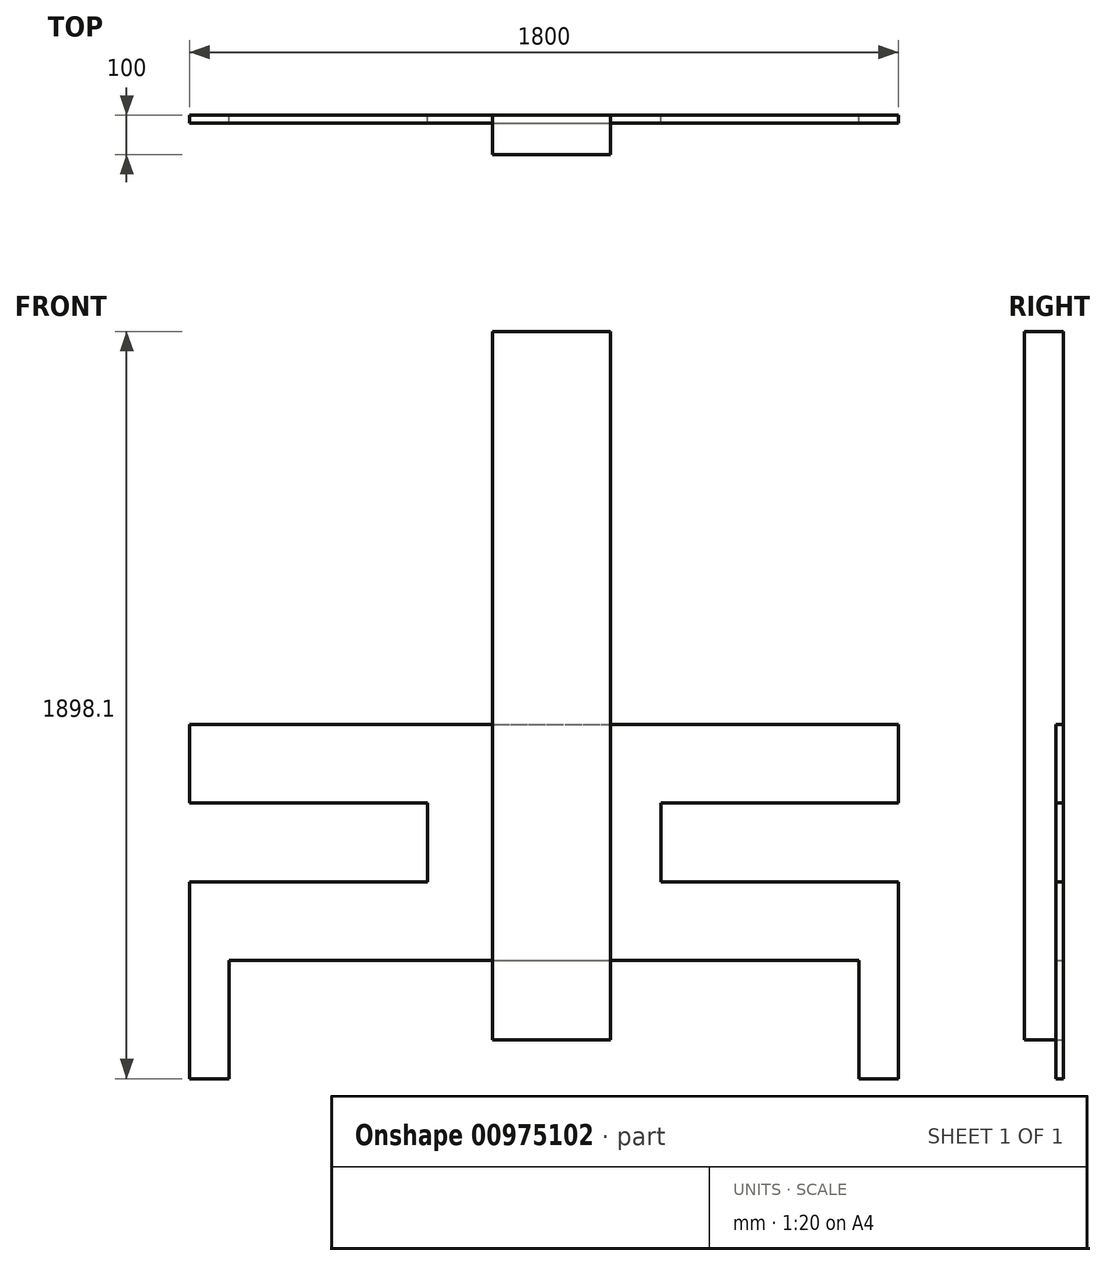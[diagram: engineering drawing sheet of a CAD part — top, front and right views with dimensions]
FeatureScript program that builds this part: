
annotation { "Feature Type Name" : "Feature", "Feature Type Description" : "" }
export const myFeature = defineFeature(function(context is Context, id is Id, definition is map)
    precondition{}
    {
        {
            var Q0;
            Q0=qCreatedBy(makeId("Front.planeOp"),FACE);
            var sketch = newSketch(context, id + "F0", { "sketchPlane" : qUnion([Q0])});
            skLineSegment(sketch, "E0.bottom", {"start": v(-150, 900) * mm, "end": v(150, 900) * mm});
            skLineSegment(sketch, "E0.top", {"start": v(-150, -900) * mm, "end": v(150, -900) * mm});
            skLineSegment(sketch, "E0.left", {"start": v(-150, 900) * mm, "end": v(-150, -900) * mm});
            skLineSegment(sketch, "E0.right", {"start": v(150, 900) * mm, "end": v(150, -900) * mm});
            skPoint(sketch, "E0.middle", {"position": v(0, 0) * mm});
            skSolve(sketch);
        }
        {
            var Q0;
            Q0=makeQuery(id+"F0.imprint","IMPRINT",FACE,{"disambiguationData":[TD([[makeQuery(id+"F0.imprint","IMPRINT",EDGE,{"derivedFrom":sQuery(id+"F0.wireOp",EDGE,"E0.bottom")}),-1.0]])]});
            extrude(context, id + "F1", {"entities" : qUnion([Q0]), "depth" : 100 * mm, "offsetDistance" : 25 * mm});
        }
        {
            var Q0;
            Q0=qCreatedBy(makeId("Front.planeOp"),FACE);
            var sketch = newSketch(context, id + "F2", { "sketchPlane" : qUnion([Q0])});
            skLineSegment(sketch, "E1.left", {"start": v(-315.18, -298.1) * mm, "end": v(-315.18, -498.1) * mm});
            skLineSegment(sketch, "E1.right", {"start": v(277.84, -298.1) * mm, "end": v(277.84, -498.1) * mm});
            skPoint(sketch, "E1.middle", {"position": v(0, 0) * mm});
            skLineSegment(sketch, "E2", {"start": v(-315.18, -298.1) * mm, "end": v(-918.67, -298.1) * mm});
            skLineSegment(sketch, "E3", {"start": v(-918.67, -298.1) * mm, "end": v(-918.67, -98.1) * mm});
            skLineSegment(sketch, "E4", {"start": v(-918.67, -98.1) * mm, "end": v(881.33, -98.1) * mm});
            skLineSegment(sketch, "E5", {"start": v(881.33, -98.1) * mm, "end": v(881.33, -298.1) * mm});
            skLineSegment(sketch, "E6", {"start": v(881.33, -298.1) * mm, "end": v(277.84, -298.1) * mm});
            skLineSegment(sketch, "E7", {"start": v(-315.18, -498.1) * mm, "end": v(-918.67, -498.1) * mm});
            skLineSegment(sketch, "E8", {"start": v(-918.67, -498.1) * mm, "end": v(-918.67, -998.1) * mm});
            skLineSegment(sketch, "E9", {"start": v(-918.67, -998.1) * mm, "end": v(-818.67, -998.1) * mm});
            skLineSegment(sketch, "E10", {"start": v(-818.67, -998.1) * mm, "end": v(-818.67, -698.1) * mm});
            skLineSegment(sketch, "E11", {"start": v(781.33, -698.1) * mm, "end": v(781.33, -998.1) * mm});
            skLineSegment(sketch, "E12", {"start": v(781.33, -998.1) * mm, "end": v(881.33, -998.1) * mm});
            skLineSegment(sketch, "E13", {"start": v(881.33, -998.1) * mm, "end": v(881.33, -498.1) * mm});
            skLineSegment(sketch, "E14", {"start": v(881.33, -498.1) * mm, "end": v(277.84, -498.1) * mm});
            skLineSegment(sketch, "E15", {"start": v(-818.67, -698.1) * mm, "end": v(781.33, -698.1) * mm});
            skLineSegment(sketch, "E16", {"start": v(-918.67, -298.1) * mm, "end": v(-918.67, -498.1) * mm, "construction": true});
            skLineSegment(sketch, "E17", {"start": v(881.33, -298.1) * mm, "end": v(881.33, -498.1) * mm, "construction": true});
            skLineSegment(sketch, "E18", {"start": v(-818.67, -998.1) * mm, "end": v(781.33, -998.1) * mm, "construction": true});
            skSolve(sketch);
        }
        {
            var Q0;
            Q0 = qSketchRegion(id + "F2", true);
            extrude(context, id + "F3", {"entities" : qUnion([Q0]), "depth" : 20 * mm, "offsetDistance" : 25 * mm});
        }
    });
